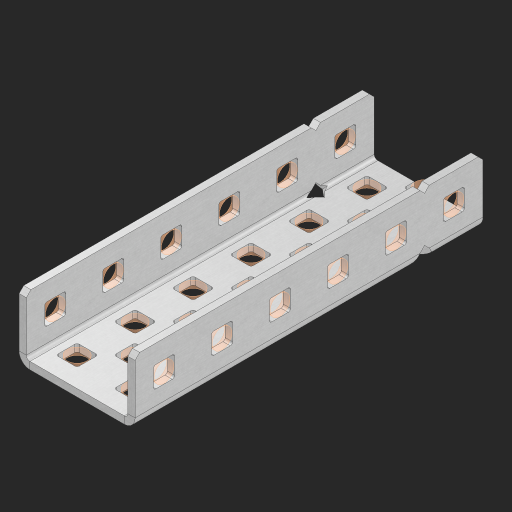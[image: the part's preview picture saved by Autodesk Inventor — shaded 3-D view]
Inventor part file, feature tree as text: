
AUTODESK INVENTOR PART (.ipt)
format: ipt  version: 2023 (Build 270158000, 158)  size: 703,488 bytes
history: native  units: in
note: dims shown in document units (in); Inventor stores cm internally (conversion verified against a paired STEP export)
features: other x37, extrude x28, sheet_metal_op x11, sketch x10, pattern_linear x2, mirror x1, chamfer x1
ambient origin geometry x8: Origin, YZ Plane, XZ Plane, XY Plane, X Axis, Y Axis, Z Axis, Center Point
bodies: Solid1 (feature_tree), Body (feature_tree)
feature tree (90):
  sheet_metal_op  "Flanges"
  other  "Flange Pattern Plane"
  other  "Flange Pattern Sketch"
  sheet_metal_op  "Flange Pattern"
  sheet_metal_op  "Body Pattern"
  pattern_linear  "Center Pattern"  Spacing1=0.0625in  [1 undecoded]
  other  "Arc Length"
  mirror  "Notch Mirror"
  pattern_linear  "Notch Pattern"  Spacing1=0.182in  [1 undecoded]
  chamfer  "End Chamfer"
  extrude  "Half Cut"  Depth=0.02in
  sketch  "Sketch1"  dims[d0=1.0in]
  other  "Plate1"
  sketch  "Sketch2"  dims[d1=3.0in]
  other  "Plate2"
  sheet_metal_op  "Bend1"
  sheet_metal_op  "Corner1"
  sketch  "Sketch3"  dims[d2=0.0625in]
  sketch  "Sketch7"  dims[d3=0.0625in]
  other  "Srf1"
  other  "Srf2"
  sketch  "Sketch8"  dims[d4=0.0312in]
  sketch  "Sketch9"  dims[d5=0.125in]
  other  "Srf91"
  sheet_metal_op  "Body Pattern Sketch"
  other  "Srf92"
  sketch  "Sketch13"  dims[d6=0.0625in]
  sketch  "Sketch14"  dims[d7=0.5in d8=90.0deg d9=0.0312in]
  sketch  "Sketch15"  dims[d10=0.25in]
  sketch  "Sketch16"  dims[d11=0.0625in d12=0.0625in d16=0.182in d17=0.02in d18=0.0625in d19=0.0in d20=0.25in d21=0.25in d38=2.3622in d40=0.5in d41=0.7874in d43=1.0in d46=0.172in d47=1.0in d48=0.0in d49=0.182in d50=0.02in d51=0.25in d52=0.25in d53=0.0625in d54=0.0in d55=0.172in d56=1.0in d57=0.0in d58=0.25in d60=2.3622in d62=0.5in d63=0.7874in d65=0.5in d85=0.1473in d86=0.1782in d88=0.04in d89=0.0625in d90=0.0in d91=0.04in d92=0.0491in d95=2.5in d96=0.04in d97=0.25in d98=45.0deg d99=0.25in d100=0.5in d101=0.0in d102=2.497in d106=0.182in d107=0.02in d108=0.5in d109=0.5in d110=0.0625in d111=0.0in d112=0.172in d113=0.5in d114=0.0in d117=0.5in d118=0.5in d119=0.5in]
  other  "Srf786"
  other  "Srf823"
  other  "Srf824"
  other  "Srf825"
  other  "Srf826"
  other  "Srf827"
  other  "Srf828"
  other  "Srf829"
  other  "Srf856"
  other  "Srf857"
  other  "Srf858"
  other  "Srf859"
  other  "Srf860"
  other  "Srf861"
  other  "Srf862"
  other  "Srf889"
  other  "Srf890"
  other  "Srf891"
  other  "Srf892"
  other  "Srf893"
  other  "Srf922"
  other  "Srf923"
  other  "Srf924"
  other  "Srf959"
  other  "Srf960"
  other  "Srf961"
  sheet_metal_op  "Flange Stamp"
  sheet_metal_op  "Flange Circle"
  sheet_metal_op  "Body Stamp"
  sheet_metal_op  "Body Circle"
  other  "Center Stamp"
  other  "Center Circle"
  sheet_metal_op  "Notch"
  extrude  "ExtrusionSrf2"  Depth=0.0625in
  extrude  "ExtrusionSrf92"  TaperAngle=0.0deg  [1 undecoded]
  extrude  "ExtrusionSrf823"  Depth=0.5in
  extrude  "ExtrusionSrf824"  Depth=0.5in
  extrude  "ExtrusionSrf825"  Depth=0.5in
  extrude  "ExtrusionSrf826"  Depth=0.5in
  extrude  "ExtrusionSrf827"  Depth=1.0in TaperAngle=0.0deg
  extrude  "ExtrusionSrf828"  Depth=0.5in
  extrude  "ExtrusionSrf829"  Depth=0.02in
  extrude  "ExtrusionSrf856"  Depth=0.5in
  extrude  "ExtrusionSrf857"  Depth=0.5in
  extrude  "ExtrusionSrf858"  Depth=0.0625in
  extrude  "ExtrusionSrf859"  TaperAngle=0.0deg  [1 undecoded]
  extrude  "ExtrusionSrf860"  Depth=0.5in
  extrude  "ExtrusionSrf861"  Depth=1.0in TaperAngle=0.0deg
  extrude  "ExtrusionSrf862"  Depth=0.5in
  extrude  "ExtrusionSrf889"  Depth=0.5in
  extrude  "ExtrusionSrf890"  Depth=0.5in
  extrude  "ExtrusionSrf891"  Depth=0.5in
  extrude  "ExtrusionSrf892"  Depth=0.5in
  extrude  "ExtrusionSrf893"  Depth=0.5in
  extrude  "ExtrusionSrf922"  Depth=0.0625in
  extrude  "ExtrusionSrf923"  TaperAngle=0.0deg  [1 undecoded]
  extrude  "ExtrusionSrf924"  Depth=0.5in
  extrude  "ExtrusionSrf959"  Depth=0.5in
  extrude  "ExtrusionSrf960"  Depth=2.5in
  extrude  "ExtrusionSrf961"  Depth=0.5in TaperAngle=45.0deg
note: 5 required parameter values undecoded (feature->parameter linkage not recoverable at this tier; creation-order binding heuristic only, values carry confidence <= 0.55)
